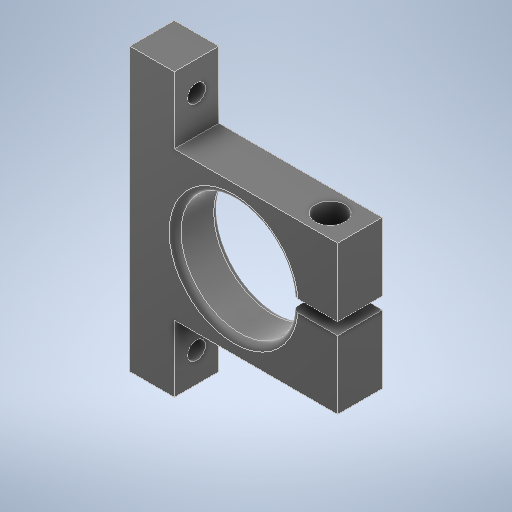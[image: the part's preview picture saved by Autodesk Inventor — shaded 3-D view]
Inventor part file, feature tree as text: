
AUTODESK INVENTOR PART (.ipt)
format: ipt  version: 2025.1 (Build 291241020, 241B)  size: 521,216 bytes
history: native  units: mm
features: sketch x5, extrude x3, mirror x3, hole x2, fillet x1
ambient origin geometry x8: Origin, YZ Plane, XZ Plane, XY Plane, X Axis, Y Axis, Z Axis, Center Point
bodies: Solid1 (feature_tree)
feature tree (14):
  extrude  "Extrusion1"  Depth=25.0mm
  mirror  "Mirror1"
  extrude  "Extrusion2"  Depth=15.0mm TaperAngle=0.0deg
  hole  "Hole1"  [1 undecoded]
  extrude  "Extrusion3"  Depth=2.0mm
  mirror  "Mirror2"
  hole  "Hole2"  [1 undecoded]
  mirror  "Mirror3"
  fillet  "Fillet1"  Radius=10.0mm
  sketch  "Sketch1"  dims[d0=15.0mm d1=25.0mm]
  sketch  "Sketch2"  dims[d2=47.5mm d4=15.0mm d5=0.0mm]
  sketch  "Sketch3"  dims[d6=39.5mm d7=35.0mm]
  sketch  "Sketch4"  dims[d8=4.0mm d9=2.0mm]
  sketch  "Sketch5"  dims[d10=5.0mm d11=0.0mm d12=7.5mm d13=10.0mm d14=6.0mm d15=6.0mm d16=4.0mm d17=2.0mm d18=90.0deg d19=8.0mm d20=20.594885mm d21=10.0mm d22=15.0mm d23=0.0mm d24=55.0mm d26=7.5mm d27=6.0mm d28=6.0mm d29=4.0mm d30=2.0mm d31=90.0deg d32=8.0mm d33=20.594885mm d34=10.0mm d35=2.0mm]
note: 2 required parameter values undecoded (feature->parameter linkage not recoverable at this tier; creation-order binding heuristic only, values carry confidence <= 0.55)
